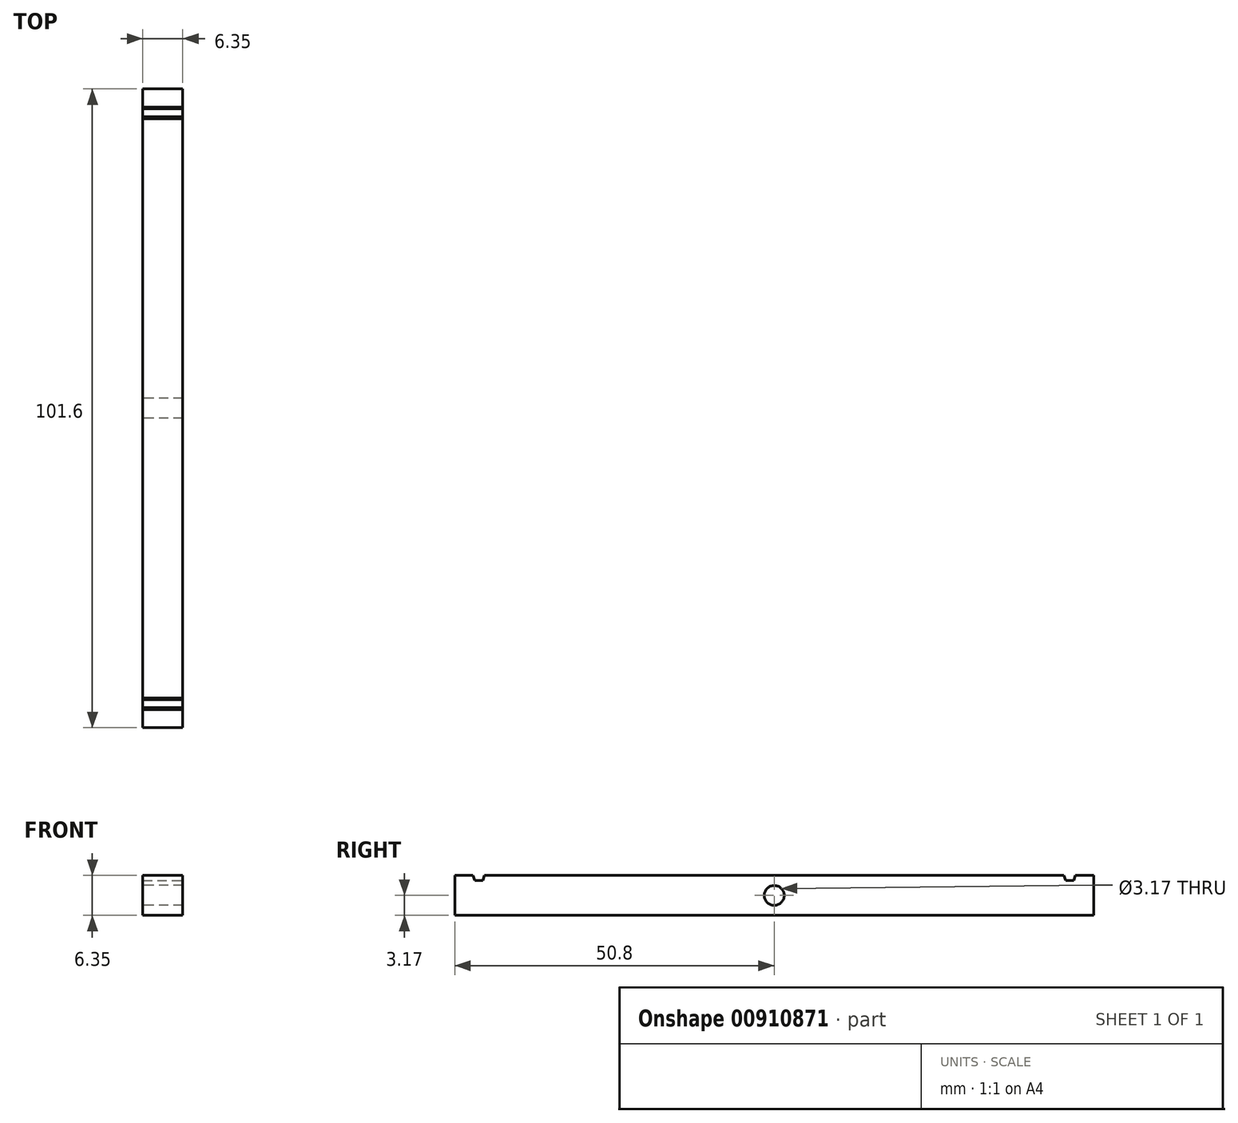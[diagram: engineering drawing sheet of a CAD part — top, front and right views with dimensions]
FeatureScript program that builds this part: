
annotation { "Feature Type Name" : "Feature", "Feature Type Description" : "" }
export const myFeature = defineFeature(function(context is Context, id is Id, definition is map)
    precondition{}
    {
        {
            var Q0;
            Q0=qCreatedBy(makeId("Right.planeOp"),FACE);
            var sketch = newSketch(context, id + "F0", { "sketchPlane" : qUnion([Q0])});
            skLineSegment(sketch, "E0.bottom", {"start": v(-50.8, 3.18) * mm, "end": v(50.8, 3.18) * mm});
            skLineSegment(sketch, "E0.top", {"start": v(-50.8, -3.18) * mm, "end": v(50.8, -3.18) * mm});
            skLineSegment(sketch, "E0.left", {"start": v(-50.8, 3.18) * mm, "end": v(-50.8, -3.18) * mm});
            skLineSegment(sketch, "E0.right", {"start": v(50.8, 3.18) * mm, "end": v(50.8, -3.18) * mm});
            skCircle(sketch, "E1", {"center": v(0, 0) * mm, "radius": 1.59 * mm});
            skSolve(sketch);
        }
        {
            var Q0;
            Q0=makeQuery(id+"F0.imprint","IMPRINT",FACE,{"disambiguationData":[TD([[makeQuery(id+"F0.imprint","IMPRINT",EDGE,{"derivedFrom":sQuery(id+"F0.wireOp",EDGE,"E0.bottom")}),-1.0]])]});
            extrude(context, id + "F1", {"entities" : qUnion([Q0]), "depth" : 6.35 * mm, "offsetDistance" : 25.4 * mm});
        }
        {
            var Q0;
            Q0=makeQuery(id+"F1.opExtrude","CAP_FACE",FACE,{"disambiguationData":[OSD([sQuery(id+"F0.wireOp",EDGE,"E0.bottom"),sQuery(id+"F0.wireOp",EDGE,"E0.top"),sQuery(id+"F0.wireOp",EDGE,"E0.left"),sQuery(id+"F0.wireOp",EDGE,"E0.right"),sQuery(id+"F0.wireOp",EDGE,"E1")])],"isStart":false});
            var sketch = newSketch(context, id + "F2", { "sketchPlane" : qUnion([Q0])});
            skLineSegment(sketch, "E2", {"start": v(0, 0) * mm, "end": v(0, 10.88) * mm, "construction": true});
            skLineSegment(sketch, "E3", {"start": v(-47.62, 2.4) * mm, "end": v(-48.65, 5.15) * mm});
            skLineSegment(sketch, "E4", {"start": v(-48.65, 5.15) * mm, "end": v(-45.33, 5.15) * mm});
            skLineSegment(sketch, "E5", {"start": v(-45.33, 5.15) * mm, "end": v(-46.36, 2.4) * mm});
            skLineSegment(sketch, "E6", {"start": v(-46.36, 2.4) * mm, "end": v(-47.63, 2.4) * mm});
            skLineSegment(sketch, "E7", {"start": v(-47.63, 2.4) * mm, "end": v(-50.8, 2.4) * mm});
            skLineSegment(sketch, "E8.MirrorCS", {"start": v(46.36, 2.4) * mm, "end": v(47.63, 2.4) * mm});
            skLineSegment(sketch, "E9.MirrorCS", {"start": v(45.33, 5.15) * mm, "end": v(46.36, 2.4) * mm});
            skLineSegment(sketch, "E10.MirrorCS", {"start": v(47.63, 2.4) * mm, "end": v(50.8, 2.4) * mm});
            skLineSegment(sketch, "E11.MirrorCS", {"start": v(47.62, 2.4) * mm, "end": v(48.65, 5.15) * mm});
            skLineSegment(sketch, "E12.MirrorCS", {"start": v(48.65, 5.15) * mm, "end": v(45.33, 5.15) * mm});
            skSolve(sketch);
        }
        {
            var Q0;
            Q0 = qSketchRegion(id + "F2", true);
            extrude(context, id + "F3", {"entities" : qUnion([Q0]), "operationType" : NewBodyOperationType.REMOVE, "oppositeDirection" : true, "depth" : 7.62 * mm, "offsetDistance" : 25.4 * mm});
        }
    });
